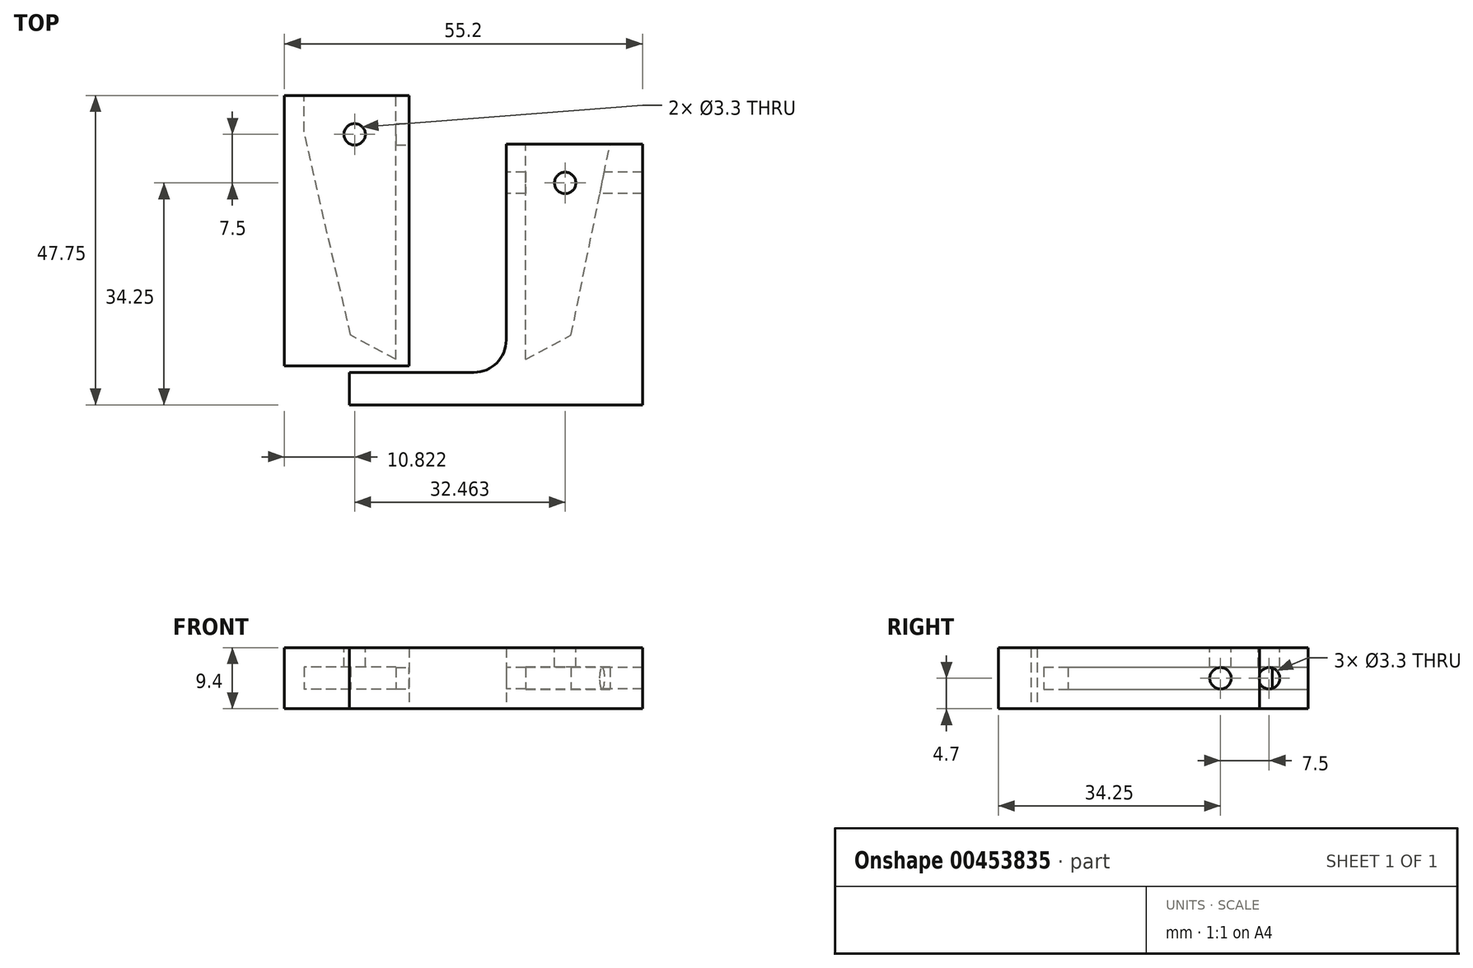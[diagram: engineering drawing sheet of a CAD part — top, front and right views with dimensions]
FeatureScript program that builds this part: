
annotation { "Feature Type Name" : "Feature", "Feature Type Description" : "" }
export const myFeature = defineFeature(function(context is Context, id is Id, definition is map)
    precondition{}
    {
        {
            var Q0;
            Q0=qCreatedBy(makeId("Top.planeOp"),FACE);
            var sketch = newSketch(context, id + "F0", { "sketchPlane" : qUnion([Q0])});
            skLineSegment(sketch, "E0", {"start": v(0, 0) * mm, "end": v(0, 40.75) * mm});
            skLineSegment(sketch, "E1", {"start": v(0, 40.75) * mm, "end": v(20, 40.75) * mm});
            skLineSegment(sketch, "E2", {"start": v(0, 0) * mm, "end": v(-14.2, 0) * mm, "construction": true});
            skLineSegment(sketch, "E3", {"start": v(0, 40.75) * mm, "end": v(0, 35.25) * mm, "construction": true});
            skLineSegment(sketch, "E4", {"start": v(0, 35.25) * mm, "end": v(-14.2, 35.25) * mm, "construction": true});
            skLineSegment(sketch, "E5", {"start": v(0, 3.75) * mm, "end": v(-7, 3.75) * mm, "construction": true});
            skLineSegment(sketch, "E6", {"start": v(0, 0) * mm, "end": v(-7, 3.75) * mm});
            skLineSegment(sketch, "E7", {"start": v(-7, 3.75) * mm, "end": v(-14.2, 35.25) * mm});
            skLineSegment(sketch, "E8", {"start": v(-14.2, 35.25) * mm, "end": v(-14.2, 40.75) * mm});
            skLineSegment(sketch, "E9", {"start": v(0, 40.75) * mm, "end": v(-14.2, 40.75) * mm});
            skLineSegment(sketch, "E10", {"start": v(10, 40.75) * mm, "end": v(10, 0) * mm, "construction": true});
            skLineSegment(sketch, "E11.MirrorCS", {"start": v(20, 40.75) * mm, "end": v(34.2, 40.75) * mm, "construction": true});
            skLineSegment(sketch, "E12.MirrorCS", {"start": v(20, 0) * mm, "end": v(20, 40.75) * mm});
            skLineSegment(sketch, "E13.MirrorCS", {"start": v(20, 0) * mm, "end": v(27, 3.75) * mm});
            skLineSegment(sketch, "E14", {"start": v(20, 33.25) * mm, "end": v(33, 33.25) * mm});
            skLineSegment(sketch, "E15", {"start": v(27, 3.75) * mm, "end": v(33, 33.25) * mm});
            skLineSegment(sketch, "E16", {"start": v(-14.2, 40.75) * mm, "end": v(-17.2, 40.75) * mm});
            skLineSegment(sketch, "E17", {"start": v(-17.2, 40.75) * mm, "end": v(-17.2, 0) * mm});
            skLineSegment(sketch, "E18", {"start": v(-17.2, 0) * mm, "end": v(0, 0) * mm});
            skLineSegment(sketch, "E19", {"start": v(20, 40.75) * mm, "end": v(17, 40.75) * mm, "construction": true});
            skLineSegment(sketch, "E20", {"start": v(17, 40.75) * mm, "end": v(17, 0) * mm});
            skLineSegment(sketch, "E21", {"start": v(17, 0) * mm, "end": v(20, 0) * mm, "construction": true});
            skLineSegment(sketch, "E22", {"start": v(17, 0) * mm, "end": v(17, -2) * mm});
            skLineSegment(sketch, "E23", {"start": v(17, -2) * mm, "end": v(-7.2, -2) * mm});
            skLineSegment(sketch, "E24", {"start": v(-17.2, -2) * mm, "end": v(-17.2, -7) * mm, "construction": true});
            skLineSegment(sketch, "E25", {"start": v(38, 33.25) * mm, "end": v(38, -7) * mm});
            skLineSegment(sketch, "E26", {"start": v(38, -7) * mm, "end": v(-7.2, -7) * mm});
            skLineSegment(sketch, "E27", {"start": v(20, 33.25) * mm, "end": v(17, 33.25) * mm});
            skLineSegment(sketch, "E28", {"start": v(33, 33.25) * mm, "end": v(38, 33.25) * mm});
            skLineSegment(sketch, "E29", {"start": v(-7.2, -2) * mm, "end": v(-7.2, -7) * mm});
            skLineSegment(sketch, "E30", {"start": v(2, 0) * mm, "end": v(2, 40.75) * mm});
            skLineSegment(sketch, "E31", {"start": v(2, 0) * mm, "end": v(2, -1) * mm});
            skLineSegment(sketch, "E32", {"start": v(2, -1) * mm, "end": v(-17.2, -1) * mm});
            skLineSegment(sketch, "E33", {"start": v(-17.2, -1) * mm, "end": v(-17.2, 0) * mm});
            skSolve(sketch);
        }
        {
            var Q0;
            Q0=makeQuery(id+"F0.imprint","IMPRINT",FACE,{"disambiguationData":[TD([[makeQuery(id+"F0.imprint","IMPRINT",EDGE,{"derivedFrom":sQuery(id+"F0.wireOp",EDGE,"E6")}),1.0]])]});
            var Q1;
            {var subQ1=sQuery(id+"F0.wireOp",EDGE,"E13.MirrorCS");Q1=makeQuery(id+"F0.imprint","IMPRINT",FACE,{"disambiguationData":[TD([[makeQuery(id+"F0.imprint","IMPRINT",EDGE,{"derivedFrom":subQ1}),-1.0]])]});}
            var Q2;
            {var subQ0=sQuery(id+"F0.wireOp",EDGE,"J3q4tp2L-M9HN-53sp-C9dw-j6FoZqq1kE6U");Q2=makeQuery(id+"F0.imprint","IMPRINT",FACE,{"disambiguationData":[TD([[makeQuery(id+"F0.imprint","IMPRINT",EDGE,{"derivedFrom":subQ0}),-1.0]])]});}
            var Q3;
            {var subQ0=sQuery(id+"F0.wireOp",EDGE,"E0");Q3=makeQuery(id+"F0.imprint","IMPRINT",FACE,{"disambiguationData":[TD([[makeQuery(id+"F0.imprint","IMPRINT",EDGE,{"derivedFrom":subQ0}),-1.0]])]});}
            extrude(context, id + "F1", {"entities" : qUnion([Q0, Q1, Q2, Q3]), "depth" : 3.4 * mm});
        }
        {
            var Q0;
            Q0=makeQuery(id+"F1.opExtrude","CAP_FACE",FACE,{"disambiguationData":[OSD([sQuery(id+"F0.wireOp",EDGE,"E12.MirrorCS"),sQuery(id+"F0.wireOp",EDGE,"E13.MirrorCS"),sQuery(id+"F0.wireOp",EDGE,"E15"),sQuery(id+"F0.wireOp",EDGE,"E20"),sQuery(id+"F0.wireOp",EDGE,"E22"),sQuery(id+"F0.wireOp",EDGE,"E23"),sQuery(id+"F0.wireOp",EDGE,"E24"),sQuery(id+"F0.wireOp",EDGE,"E25"),sQuery(id+"F0.wireOp",EDGE,"E26"),sQuery(id+"F0.wireOp",EDGE,"E27"),sQuery(id+"F0.wireOp",EDGE,"E28")])],"isStart":false});
            var sketch = newSketch(context, id + "F2", { "sketchPlane" : qUnion([Q0])});
            skLineSegment(sketch, "E34.0.0", {"start": v(20, 0) * mm, "end": v(27, 3.75) * mm});
            skLineSegment(sketch, "E34.0.1", {"start": v(27, 3.75) * mm, "end": v(33, 33.25) * mm});
            skLineSegment(sketch, "E34.0.2", {"start": v(33, 33.25) * mm, "end": v(20, 33.25) * mm});
            skLineSegment(sketch, "E34.0.3", {"start": v(20, 33.25) * mm, "end": v(20, 0) * mm});
            skLineSegment(sketch, "E35.0.0", {"start": v(20, 33.25) * mm, "end": v(17, 33.25) * mm});
            skLineSegment(sketch, "E35.0.1", {"start": v(17, 33.25) * mm, "end": v(17, -2) * mm});
            skLineSegment(sketch, "E35.0.2", {"start": v(17, -2) * mm, "end": v(17, -2) * mm});
            skLineSegment(sketch, "E35.0.4", {"start": v(38, -7) * mm, "end": v(38, -7) * mm});
            skLineSegment(sketch, "E35.0.5", {"start": v(38, -7) * mm, "end": v(38, 33.25) * mm});
            skLineSegment(sketch, "E35.0.6", {"start": v(38, 33.25) * mm, "end": v(33, 33.25) * mm});
            skLineSegment(sketch, "E35.0.7", {"start": v(33, 33.25) * mm, "end": v(27, 3.75) * mm});
            skLineSegment(sketch, "E35.0.8", {"start": v(27, 3.75) * mm, "end": v(20, 0) * mm});
            skLineSegment(sketch, "E35.0.9", {"start": v(20, 0) * mm, "end": v(20, 33.25) * mm});
            skLineSegment(sketch, "E36.0.0", {"start": v(-17.2, 40.75) * mm, "end": v(-17.2, 40.75) * mm});
            skLineSegment(sketch, "E36.0.2", {"start": v(0, 0) * mm, "end": v(-7, 3.75) * mm});
            skLineSegment(sketch, "E36.0.3", {"start": v(-7, 3.75) * mm, "end": v(-14.2, 35.25) * mm});
            skLineSegment(sketch, "E36.0.4", {"start": v(-14.2, 35.25) * mm, "end": v(-14.2, 40.75) * mm});
            skLineSegment(sketch, "E36.0.5", {"start": v(-14.2, 40.75) * mm, "end": v(-17.2, 40.75) * mm});
            skLineSegment(sketch, "E37.0.0", {"start": v(0, 0) * mm, "end": v(0, 40.75) * mm});
            skLineSegment(sketch, "E37.0.1", {"start": v(0, 40.75) * mm, "end": v(-14.2, 40.75) * mm});
            skLineSegment(sketch, "E37.0.2", {"start": v(-14.2, 40.75) * mm, "end": v(-14.2, 35.25) * mm});
            skLineSegment(sketch, "E37.0.3", {"start": v(-14.2, 35.25) * mm, "end": v(-7, 3.75) * mm});
            skLineSegment(sketch, "E37.0.4", {"start": v(-7, 3.75) * mm, "end": v(0, 0) * mm});
            skLineSegment(sketch, "E38.0.3", {"start": v(-7.2, -2) * mm, "end": v(-7.2, -7) * mm});
            skLineSegment(sketch, "E38.0.4", {"start": v(-7.2, -7) * mm, "end": v(38, -7) * mm});
            skLineSegment(sketch, "E39.0.2", {"start": v(17, -2) * mm, "end": v(-7.2, -2) * mm});
            skLineSegment(sketch, "E40.0.0", {"start": v(-17.2, 40.75) * mm, "end": v(-17.2, -1) * mm});
            skLineSegment(sketch, "E40.0.1", {"start": v(-17.2, -1) * mm, "end": v(2, -1) * mm});
            skLineSegment(sketch, "E40.0.2", {"start": v(2, -1) * mm, "end": v(2, 40.75) * mm});
            skLineSegment(sketch, "E41.0.0", {"start": v(0, 40.75) * mm, "end": v(0, 0) * mm});
            skLineSegment(sketch, "E41.0.2", {"start": v(2, 0) * mm, "end": v(2, 40.75) * mm});
            skLineSegment(sketch, "E41.0.3", {"start": v(2, 40.75) * mm, "end": v(0, 40.75) * mm});
            skSolve(sketch);
        }
        {
            var Q0;
            Q0=makeQuery(id+"F2.imprint","IMPRINT",FACE,{"disambiguationData":[TD([[makeQuery(id+"F2.imprint","IMPRINT",EDGE,{"derivedFrom":sQuery(id+"F2.wireOp",EDGE,"E40.0.0")}),1.0]])]});
            var Q1;
            Q1=makeQuery(id+"F2.imprint","IMPRINT",FACE,{"disambiguationData":[TD([[makeQuery(id+"F2.imprint","IMPRINT",EDGE,{"derivedFrom":sQuery(id+"F2.wireOp",EDGE,"E37.0.0")}),1.0]])]});
            var Q2;
            Q2=makeQuery(id+"F2.imprint","IMPRINT",FACE,{"disambiguationData":[TD([[makeQuery(id+"F2.imprint","IMPRINT",EDGE,{"derivedFrom":sQuery(id+"F2.wireOp",EDGE,"E35.0.0")}),1.0]])]});
            var Q3;
            Q3=makeQuery(id+"F2.imprint","IMPRINT",FACE,{"disambiguationData":[TD([[makeQuery(id+"F2.imprint","IMPRINT",EDGE,{"derivedFrom":sQuery(id+"F2.wireOp",EDGE,"E34.0.0")}),1.0]])]});
            var Q4;
            Q4=makeQuery(id+"F2.imprint","IMPRINT",FACE,{"disambiguationData":[TD([[makeQuery(id+"F2.imprint","IMPRINT",EDGE,{"derivedFrom":sQuery(id+"F2.wireOp",EDGE,"E37.0.1")}),1.0]])]});
            var Q5;
            Q5=makeQuery(id+"F2.imprint","IMPRINT",FACE,{"disambiguationData":[TD([[makeQuery(id+"F2.imprint","IMPRINT",EDGE,{"derivedFrom":sQuery(id+"F2.wireOp",EDGE,"E41.0.0")}),1.0]])]});
            extrude(context, id + "F3", {"entities" : qUnion([Q0, Q1, Q2, Q3, Q4, Q5]), "operationType" : NewBodyOperationType.ADD, "depth" : 3 * mm});
        }
        {
            var Q0;
            Q0=makeQuery(id+"F0.imprint","IMPRINT",FACE,{"disambiguationData":[TD([[makeQuery(id+"F0.imprint","IMPRINT",EDGE,{"derivedFrom":sQuery(id+"F0.wireOp",EDGE,"E6")}),1.0]])]});
            var Q1;
            Q1=makeQuery(id+"F0.imprint","IMPRINT",FACE,{"disambiguationData":[TD([[makeQuery(id+"F0.imprint","IMPRINT",EDGE,{"derivedFrom":sQuery(id+"F0.wireOp",EDGE,"E0")}),1.0]])]});
            var Q2;
            {var subQ0=sQuery(id+"F0.wireOp",EDGE,"E0");Q2=makeQuery(id+"F0.imprint","IMPRINT",FACE,{"disambiguationData":[TD([[makeQuery(id+"F0.imprint","IMPRINT",EDGE,{"derivedFrom":subQ0}),-1.0]])]});}
            extrude(context, id + "F4", {"entities" : qUnion([Q0, Q1, Q2]), "operationType" : NewBodyOperationType.ADD, "oppositeDirection" : true, "depth" : 3 * mm});
        }
        {
            var Q0;
            {var subQ2=sQuery(id+"F0.wireOp",EDGE,"E13.MirrorCS");Q0=makeQuery(id+"F0.imprint","IMPRINT",FACE,{"disambiguationData":[TD([[makeQuery(id+"F0.imprint","IMPRINT",EDGE,{"derivedFrom":subQ2}),-1.0]])]});}
            var Q1;
            {var subQ0=sQuery(id+"F0.wireOp",EDGE,"E13.MirrorCS");Q1=makeQuery(id+"F0.imprint","IMPRINT",FACE,{"disambiguationData":[TD([[makeQuery(id+"F0.imprint","IMPRINT",EDGE,{"derivedFrom":subQ0}),1.0]])]});}
            extrude(context, id + "F5", {"entities" : qUnion([Q0, Q1]), "operationType" : NewBodyOperationType.ADD, "oppositeDirection" : true, "depth" : 3 * mm});
        }
        {
            var Q0;
            Q0=makeQuery(id+"F3.opExtrude","CAP_FACE",FACE,{"disambiguationData":[OSD([sQuery(id+"F2.wireOp",EDGE,"E37.0.1"),sQuery(id+"F2.wireOp",EDGE,"E40.0.0"),sQuery(id+"F2.wireOp",EDGE,"E40.0.1"),sQuery(id+"F2.wireOp",EDGE,"E40.0.2"),sQuery(id+"F2.wireOp",EDGE,"E36.0.5"),sQuery(id+"F2.wireOp",EDGE,"E41.0.2"),sQuery(id+"F2.wireOp",EDGE,"E41.0.3")])],"isStart":false});
            var sketch = newSketch(context, id + "F6", { "sketchPlane" : qUnion([Q0])});
            skCircle(sketch, "E42", {"center": v(-6.38, 34.75) * mm, "radius": 1.65 * mm});
            skCircle(sketch, "E43", {"center": v(26.09, 27.25) * mm, "radius": 1.65 * mm});
            skSolve(sketch);
        }
        {
            var Q0;
            Q0=makeQuery(id+"F6.imprint","IMPRINT",FACE,{"disambiguationData":[TD([[makeQuery(id+"F6.imprint","IMPRINT",EDGE,{"derivedFrom":sQuery(id+"F6.wireOp",EDGE,"E42")}),1.0]])]});
            var Q1;
            Q1=makeQuery(id+"F6.imprint","IMPRINT",FACE,{"disambiguationData":[TD([[makeQuery(id+"F6.imprint","IMPRINT",EDGE,{"derivedFrom":sQuery(id+"F6.wireOp",EDGE,"E43")}),1.0]])]});
            extrude(context, id + "F7", {"entities" : qUnion([Q0, Q1]), "operationType" : NewBodyOperationType.REMOVE, "endBound" : BoundingType.UP_TO_NEXT, "oppositeDirection" : true, "depth" : 25 * mm});
        }
        {
            var Q0;
            {var subQ0=sQuery(id+"F0.wireOp",EDGE,"E31");var subQ1=sQuery(id+"F0.wireOp",EDGE,"E30");Q0=makeQuery(id+"F4.boolean.opBoolean","MERGE",FACE,{"derivedFrom":[makeQuery(id+"F3.boolean.opBoolean","MERGE",FACE,{"derivedFrom":[makeQuery(id+"F1.opExtrude","SWEPT_FACE",FACE,{"disambiguationData":[OSD([subQ1,subQ0])]}),makeQuery(id+"F3.opExtrude","SWEPT_FACE",FACE,{"disambiguationData":[OSD([sQuery(id+"F2.wireOp",EDGE,"E40.0.2"),sQuery(id+"F2.wireOp",EDGE,"E41.0.2")])]})]}),makeQuery(id+"F4.opExtrude","SWEPT_FACE",FACE,{"disambiguationData":[OSD([subQ1,subQ0])]})]});}
            var sketch = newSketch(context, id + "F8", { "sketchPlane" : qUnion([Q0])});
            skLineSegment(sketch, "E44", {"start": v(40.75, 1.7) * mm, "end": v(34.75, 1.7) * mm, "construction": true});
            skPoint(sketch, "E44.endSnap0", {"position": v(40.75, 1.7) * mm});
            skCircle(sketch, "E45", {"center": v(34.75, 1.7) * mm, "radius": 1.65 * mm});
            skSolve(sketch);
        }
        {
            var Q0;
            Q0=makeQuery(id+"F8.imprint","IMPRINT",FACE,{"disambiguationData":[TD([[makeQuery(id+"F8.imprint","IMPRINT",EDGE,{"derivedFrom":sQuery(id+"F8.wireOp",EDGE,"E45")}),1.0]])]});
            extrude(context, id + "F9", {"entities" : qUnion([Q0]), "operationType" : NewBodyOperationType.REMOVE, "endBound" : BoundingType.UP_TO_NEXT, "oppositeDirection" : true, "depth" : 25 * mm});
        }
        {
            var Q0;
            {var subQ0=sQuery(id+"F0.wireOp",EDGE,"E22");var subQ1=sQuery(id+"F0.wireOp",EDGE,"E20");Q0=makeQuery(id+"F5.boolean.opBoolean","MERGE",FACE,{"derivedFrom":[makeQuery(id+"F3.boolean.opBoolean","MERGE",FACE,{"derivedFrom":[makeQuery(id+"F1.opExtrude","SWEPT_FACE",FACE,{"disambiguationData":[OSD([subQ1,subQ0])]}),makeQuery(id+"F3.opExtrude","SWEPT_FACE",FACE,{"disambiguationData":[OSD([sQuery(id+"F2.wireOp",EDGE,"E35.0.1")])]})]}),makeQuery(id+"F5.opExtrude","SWEPT_FACE",FACE,{"disambiguationData":[OSD([subQ1,subQ0])]})]});}
            var sketch = newSketch(context, id + "F10", { "sketchPlane" : qUnion([Q0])});
            skLineSegment(sketch, "E46", {"start": v(-33.25, 1.7) * mm, "end": v(-27.25, 1.7) * mm, "construction": true});
            skCircle(sketch, "E47", {"center": v(-27.25, 1.7) * mm, "radius": 1.65 * mm});
            skSolve(sketch);
        }
        {
            var Q0;
            Q0=makeQuery(id+"F10.imprint","IMPRINT",FACE,{"disambiguationData":[TD([[makeQuery(id+"F10.imprint","IMPRINT",EDGE,{"derivedFrom":sQuery(id+"F10.wireOp",EDGE,"E47")}),1.0]])]});
            extrude(context, id + "F11", {"entities" : qUnion([Q0]), "operationType" : NewBodyOperationType.REMOVE, "endBound" : BoundingType.THROUGH_ALL, "oppositeDirection" : true, "depth" : 25 * mm});
        }
        {
            var Q0;
            {var subQ0=sQuery(id+"F0.wireOp",EDGE,"E23");var subQ1=sQuery(id+"F0.wireOp",EDGE,"E22");Q0=makeQuery(id+"F5.boolean.opBoolean","MERGE",EDGE,{"derivedFrom":[makeQuery(id+"F3.boolean.opBoolean","MERGE",EDGE,{"derivedFrom":[makeQuery(id+"F1.opExtrude","SWEPT_EDGE",EDGE,{"disambiguationData":[OSD([subQ1,subQ0])]}),makeQuery(id+"F3.opExtrude","SWEPT_EDGE",EDGE,{"disambiguationData":[OSD([sQuery(id+"F2.wireOp",EDGE,"E35.0.1"),sQuery(id+"F2.wireOp",EDGE,"E39.0.2")])]})]}),makeQuery(id+"F5.opExtrude","SWEPT_EDGE",EDGE,{"disambiguationData":[OSD([subQ1,subQ0])]})]});}
            fillet(context, id + "F12", {"entities" : qUnion([Q0]), "radius" : 5 * mm, "tangentPropagation" : true, "allowEdgeOverflow" : false});
        }
    });
